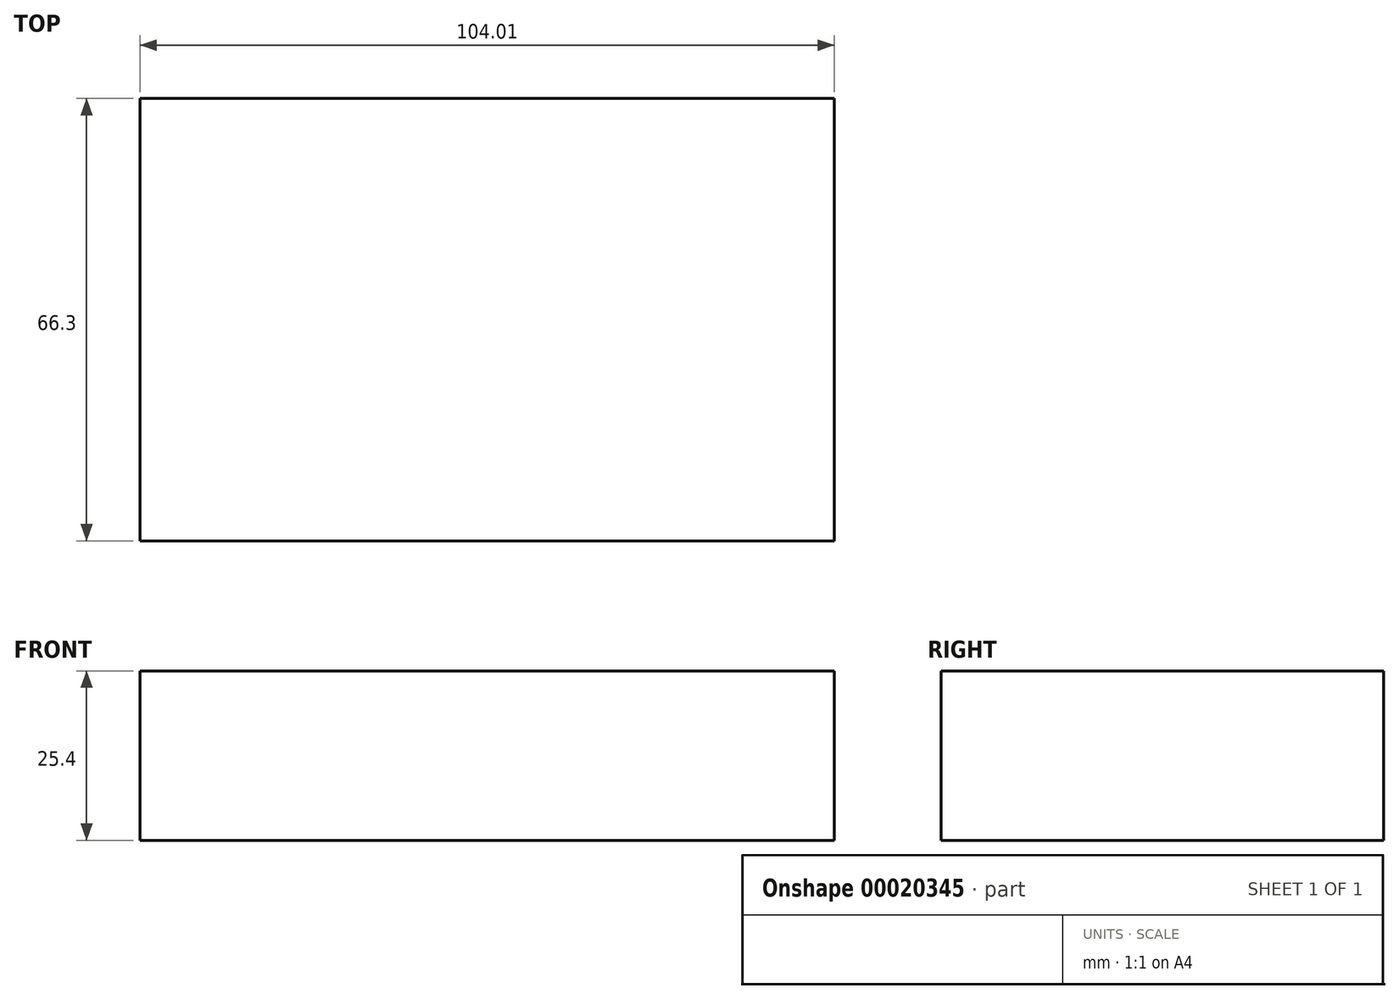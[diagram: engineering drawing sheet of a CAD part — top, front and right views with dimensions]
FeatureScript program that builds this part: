
annotation { "Feature Type Name" : "Feature", "Feature Type Description" : "" }
export const myFeature = defineFeature(function(context is Context, id is Id, definition is map)
    precondition{}
    {
        {
            var Q0;
            Q0=qCreatedBy(makeId("Top.planeOp"),FACE);
            var sketch = newSketch(context, id + "F0", { "sketchPlane" : qUnion([Q0])});
            skLineSegment(sketch, "E0.bottom", {"start": v(0, 0) * mm, "end": v(104, 0) * mm});
            skLineSegment(sketch, "E0.top", {"start": v(0, 66.3) * mm, "end": v(104, 66.3) * mm});
            skLineSegment(sketch, "E0.left", {"start": v(0, 0) * mm, "end": v(0, 66.3) * mm});
            skLineSegment(sketch, "E0.right", {"start": v(104, 0) * mm, "end": v(104, 66.3) * mm});
            skSolve(sketch);
        }
        {
            var Q0;
            Q0=makeQuery(id+"F0.imprint","IMPRINT",FACE,{"disambiguationData":[TD([[makeQuery(id+"F0.imprint","IMPRINT",EDGE,{"derivedFrom":sQuery(id+"F0.wireOp",EDGE,"E0.bottom")}),1.0]])]});
            extrude(context, id + "F1", {"entities" : qUnion([Q0]), "depth" : 25.4 * mm});
        }
    });
